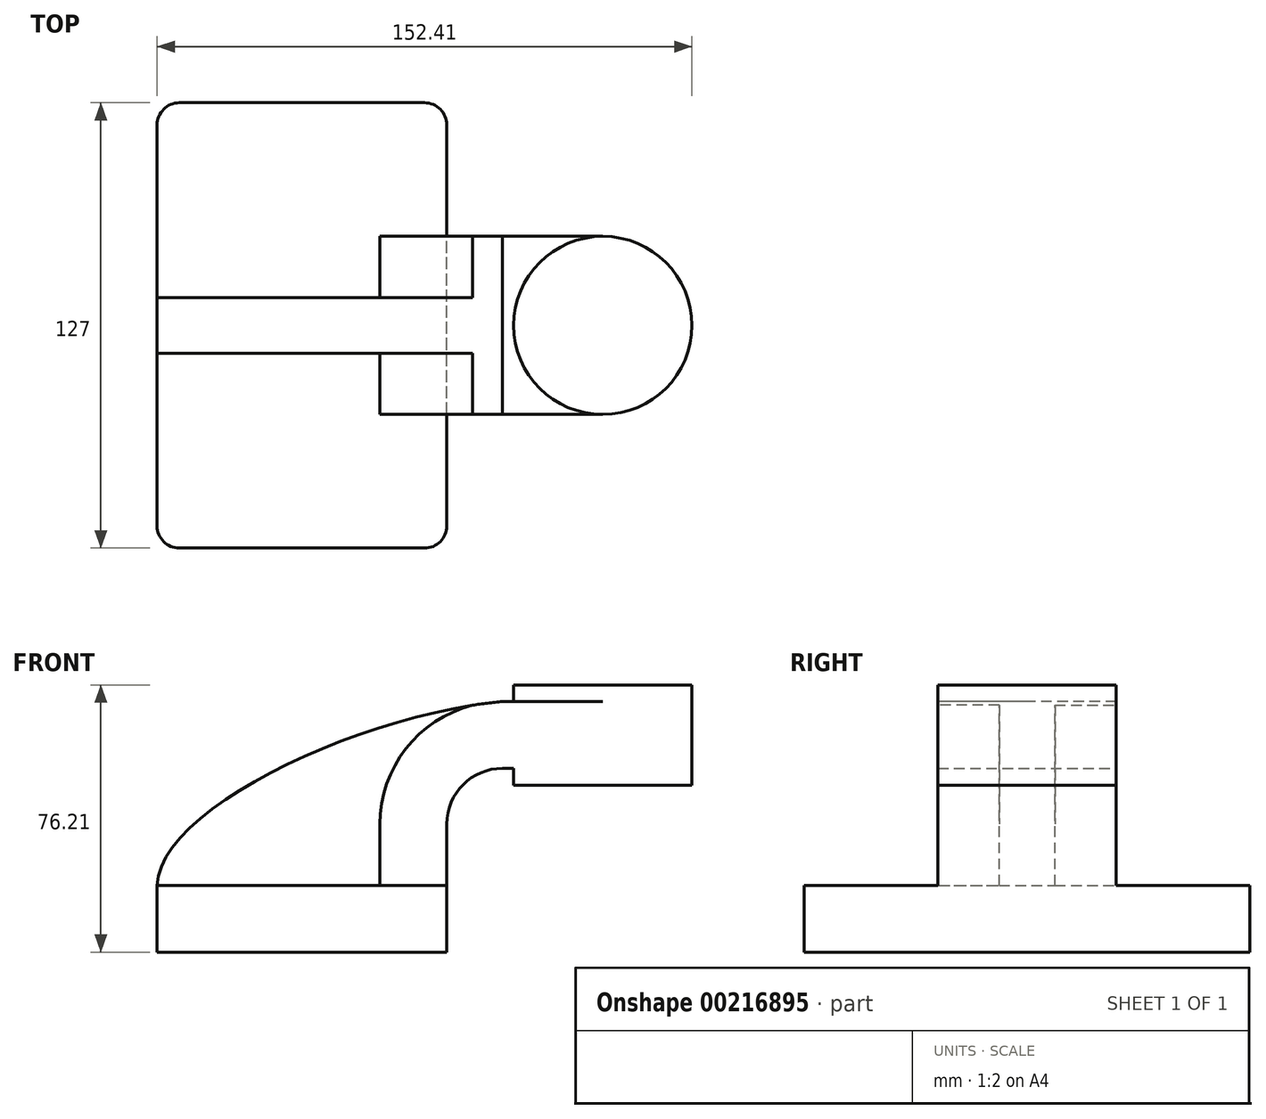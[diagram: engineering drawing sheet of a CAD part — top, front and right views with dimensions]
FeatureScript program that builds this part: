
annotation { "Feature Type Name" : "Feature", "Feature Type Description" : "" }
export const myFeature = defineFeature(function(context is Context, id is Id, definition is map)
    precondition{}
    {
        {
            var Q0;
            Q0=qCreatedBy(makeId("Front.planeOp"),FACE);
            var sketch = newSketch(context, id + "F0", { "sketchPlane" : qUnion([Q0])});
            skLineSegment(sketch, "E0.bottom", {"start": v(-41.28, 9.52) * mm, "end": v(41.27, 9.53) * mm});
            skLineSegment(sketch, "E0.top", {"start": v(-41.28, -9.53) * mm, "end": v(41.28, -9.53) * mm});
            skLineSegment(sketch, "E0.left", {"start": v(-41.28, 9.52) * mm, "end": v(-41.27, -9.53) * mm});
            skLineSegment(sketch, "E0.right", {"start": v(41.28, 9.53) * mm, "end": v(41.28, -9.52) * mm});
            skPoint(sketch, "E0.middle", {"position": v(0, 0) * mm});
            skLineSegment(sketch, "E1.bottom", {"start": v(60.33, 38.1) * mm, "end": v(111.13, 38.1) * mm});
            skLineSegment(sketch, "E1.top", {"start": v(60.33, 66.67) * mm, "end": v(111.13, 66.67) * mm});
            skLineSegment(sketch, "E1.left", {"start": v(60.33, 38.1) * mm, "end": v(60.33, 66.67) * mm});
            skLineSegment(sketch, "E1.right", {"start": v(111.13, 38.1) * mm, "end": v(111.13, 66.67) * mm});
            skPoint(sketch, "E1.middle", {"position": v(85.73, 52.39) * mm});
            skLineSegment(sketch, "E2", {"start": v(41.27, 9.53) * mm, "end": v(41.27, 27) * mm});
            skArc(sketch, "E3", {"start": v(41.28, 27) * mm, "mid": v(45.92, 38.23) * mm, "end": v(57.15, 42.88) * mm});
            skLineSegment(sketch, "E4", {"start": v(57.15, 42.88) * mm, "end": v(85.14, 42.88) * mm});
            skLineSegment(sketch, "E5.0", {"start": v(57.15, 61.93) * mm, "end": v(85.73, 61.93) * mm});
            skArc(sketch, "E5.1", {"start": v(22.23, 27) * mm, "mid": v(32.45, 51.7) * mm, "end": v(57.15, 61.93) * mm});
            skLineSegment(sketch, "E5.2", {"start": v(22.22, 9.53) * mm, "end": v(22.22, 27) * mm});
            skLineSegment(sketch, "E6", {"start": v(85.73, 38.1) * mm, "end": v(85.73, 66.67) * mm});
            skFitSpline(sketch, "E7", {"points": [v(-41.28, 9.52) * mm, v(57.15, 61.93) * mm], "startDerivative": vector(1.23, 64.7) * mm, "endDerivative": vector(123.24, 11.13) * mm});
            skSolve(sketch);
        }
        {
            var Q0;
            Q0=makeQuery(id+"F0.imprint","IMPRINT",FACE,{"disambiguationData":[TD([[makeQuery(id+"F0.imprint","IMPRINT",EDGE,{"derivedFrom":sQuery(id+"F0.wireOp",EDGE,"E0.top")}),1.0]])]});
            extrude(context, id + "F1", {"entities" : qUnion([Q0]), "endBound" : BoundingType.SYMMETRIC, "depth" : 127 * mm});
        }
        {
            var Q0;
            {var subQ5=sQuery(id+"F0.wireOp",EDGE,"E2");Q0=makeQuery(id+"F0.imprint","IMPRINT",FACE,{"disambiguationData":[TD([[makeQuery(id+"F0.imprint","IMPRINT",EDGE,{"derivedFrom":subQ5}),1.0]])]});}
            var Q1;
            {var subQ3=sQuery(id+"F0.wireOp",EDGE,"E1.left");var subQ6=sQuery(id+"F0.wireOp",EDGE,"E1.bottom");var subQ7=makeQuery(id+"F0.imprint","INTERSECT",VERTEX,{"derivedFrom":[subQ6,subQ3]});Q1=makeQuery(id+"F0.imprint","IMPRINT",FACE,{"disambiguationData":[TD([[makeQuery(id+"F0.imprint","IMPRINT",EDGE,{"disambiguationData":[TD([[subQ7,-1.0]])],"derivedFrom":subQ6}),1.0]])]});}
            extrude(context, id + "F2", {"entities" : qUnion([Q0, Q1]), "operationType" : NewBodyOperationType.ADD, "endBound" : BoundingType.SYMMETRIC, "depth" : 50.8 * mm});
        }
        {
            var Q0;
            {var subQ3=sQuery(id+"F0.wireOp",EDGE,"E5.2");Q0=makeQuery(id+"F0.imprint","IMPRINT",FACE,{"disambiguationData":[TD([[makeQuery(id+"F0.imprint","IMPRINT",EDGE,{"derivedFrom":subQ3}),1.0]])]});}
            extrude(context, id + "F3", {"entities" : qUnion([Q0]), "operationType" : NewBodyOperationType.ADD, "endBound" : BoundingType.SYMMETRIC, "depth" : 15.88 * mm});
        }
        {
            var Q0;
            {var subQ0=sQuery(id+"F0.wireOp",EDGE,"E1.right");Q0=makeQuery(id+"F0.imprint","IMPRINT",FACE,{"disambiguationData":[TD([[makeQuery(id+"F0.imprint","IMPRINT",EDGE,{"derivedFrom":subQ0}),1.0]])]});}
            var Q1;
            Q1=sQuery(id+"F0.wireOp",EDGE,"E6");
            revolve(context, id + "F4", {"operationType" : NewBodyOperationType.ADD, "entities" : qUnion([Q0]), "axis" : qUnion([Q1]), "revolveType" : RevolveType.FULL});
        }
        {
            var Q0;
            Q0=makeQuery(id+"F1.opExtrude","CAP_EDGE",EDGE,{"disambiguationData":[OSD([sQuery(id+"F0.wireOp",EDGE,"E0.left")])],"isStart":false});
            var Q1;
            Q1=makeQuery(id+"F1.opExtrude","CAP_EDGE",EDGE,{"disambiguationData":[OSD([sQuery(id+"F0.wireOp",EDGE,"E0.right")])],"isStart":false});
            var Q2;
            Q2=makeQuery(id+"F1.opExtrude","CAP_EDGE",EDGE,{"disambiguationData":[OSD([sQuery(id+"F0.wireOp",EDGE,"E0.right")])],"isStart":true});
            var Q3;
            Q3=makeQuery(id+"F1.opExtrude","CAP_EDGE",EDGE,{"disambiguationData":[OSD([sQuery(id+"F0.wireOp",EDGE,"E0.left")])],"isStart":true});
            fillet(context, id + "F5", {"entities" : qUnion([Q0, Q1, Q2, Q3]), "radius" : 6.35 * mm, "tangentPropagation" : true, "allowEdgeOverflow" : false});
        }
    });
